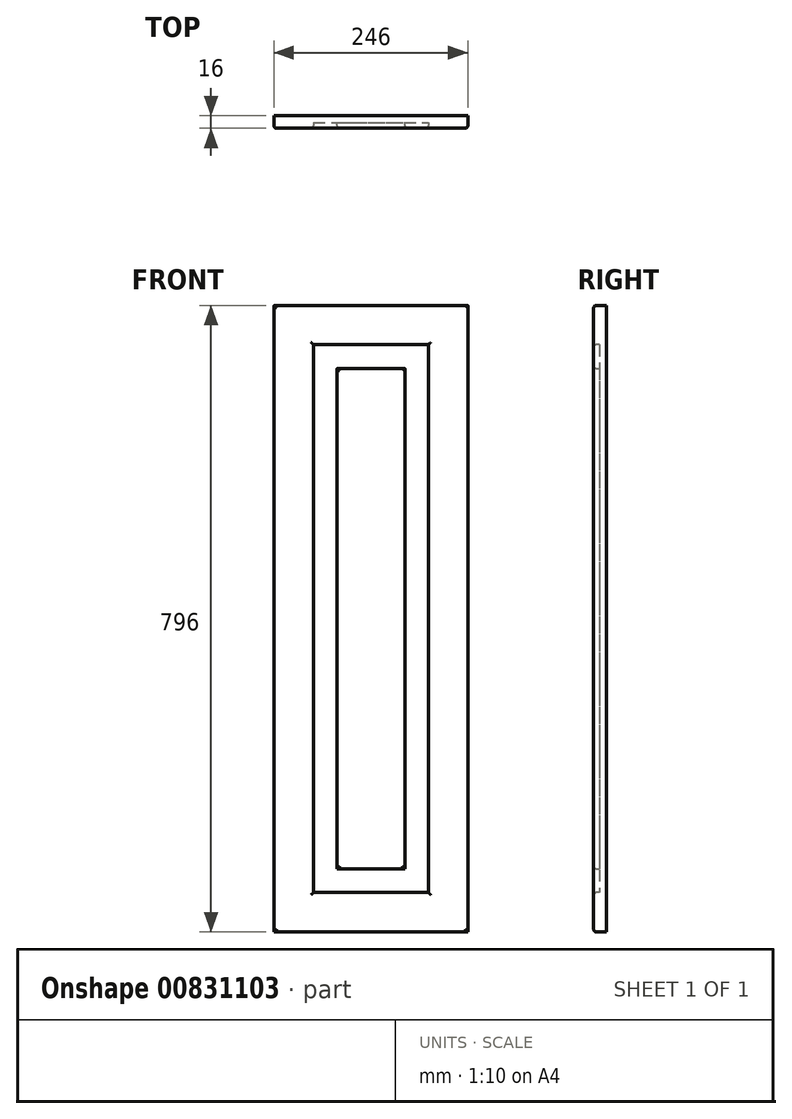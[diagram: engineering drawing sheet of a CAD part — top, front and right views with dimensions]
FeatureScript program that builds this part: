
annotation { "Feature Type Name" : "Feature", "Feature Type Description" : "" }
export const myFeature = defineFeature(function(context is Context, id is Id, definition is map)
    precondition{}
    {
        {
            var Q0;
            Q0=qCreatedBy(makeId("Front.planeOp"),FACE);
            var sketch = newSketch(context, id + "F0", { "sketchPlane" : qUnion([Q0])});
            skLineSegment(sketch, "E0.bottom", {"start": v(0, 0) * mm, "end": v(44.66, 0) * mm});
            skLineSegment(sketch, "E0.top", {"start": v(0, 33.8) * mm, "end": v(44.66, 33.8) * mm});
            skLineSegment(sketch, "E0.left", {"start": v(0, 0) * mm, "end": v(0, 33.8) * mm});
            skLineSegment(sketch, "E0.right", {"start": v(44.66, 0) * mm, "end": v(44.66, 33.8) * mm});
            skSolve(sketch);
        }
        {
            var Q0;
            Q0=makeQuery(id+"F0.imprint","IMPRINT",FACE,{"disambiguationData":[TD([[makeQuery(id+"F0.imprint","IMPRINT",EDGE,{"derivedFrom":sQuery(id+"F0.wireOp",EDGE,"E0.bottom")}),1.0]])]});
            extrude(context, id + "F1", {"entities" : qUnion([Q0]), "depth" : 16 * mm, "offsetDistance" : 25.4 * mm});
        }
        {
            var Q0;
            Q0=makeQuery(id+"F1.opExtrude","SWEPT_FACE",FACE,{"disambiguationData":[OSD([sQuery(id+"F0.wireOp",EDGE,"E0.bottom")])]});
            extrude(context, id + "F2", {"entities" : qUnion([Q0]), "operationType" : NewBodyOperationType.ADD, "oppositeDirection" : true, "depth" : 796 * mm, "offsetDistance" : 25 * mm});
        }
        {
            var Q0;
            {var subQ0=sQuery(id+"F0.wireOp",EDGE,"E0.left");Q0=makeQuery(id+"F2.boolean.opBoolean","MERGE",FACE,{"derivedFrom":[makeQuery(id+"F1.opExtrude","SWEPT_FACE",FACE,{"disambiguationData":[OSD([subQ0])]}),makeQuery(id+"F2.opExtrude","SWEPT_FACE",FACE,{"disambiguationData":[OSD([sQuery(id+"F0.wireOp",EDGE,"E0.bottom"),subQ0])]})]});}
            extrude(context, id + "F3", {"entities" : qUnion([Q0]), "operationType" : NewBodyOperationType.ADD, "oppositeDirection" : true, "depth" : 196 * mm, "offsetDistance" : 25 * mm});
        }
        {
            var Q0;
            {var subQ0=sQuery(id+"F0.wireOp",EDGE,"E0.left");var subQ1=sQuery(id+"F0.wireOp",EDGE,"E0.bottom");Q0=makeQuery(id+"F3.boolean.opBoolean","MERGE",FACE,{"derivedFrom":[makeQuery(id+"F2.boolean.opBoolean","MERGE",FACE,{"derivedFrom":[makeQuery(id+"F1.opExtrude","CAP_FACE",FACE,{"disambiguationData":[OSD([subQ1,sQuery(id+"F0.wireOp",EDGE,"E0.top"),subQ0,sQuery(id+"F0.wireOp",EDGE,"E0.right")])],"isStart":false}),makeQuery(id+"F2.opExtrude","SWEPT_FACE",FACE,{"disambiguationData":[OSD([subQ1]),TDD([makeQuery(id+"F1.opExtrude","CAP_EDGE",EDGE,{"disambiguationData":[OSD([subQ1])],"isStart":false})])]})]}),makeQuery(id+"F3.opExtrude","SWEPT_FACE",FACE,{"disambiguationData":[OSD([subQ1,subQ0]),TDD([makeQuery(id+"F2.boolean.opBoolean","MERGE",EDGE,{"derivedFrom":[makeQuery(id+"F1.opExtrude","CAP_EDGE",EDGE,{"disambiguationData":[OSD([subQ0])],"isStart":false}),makeQuery(id+"F2.opExtrude","SWEPT_EDGE",EDGE,{"disambiguationData":[OSD([subQ1,subQ0]),TDD([makeQuery(id+"F1.opExtrude","CAP_VERTEX",VERTEX,{"disambiguationData":[OSD([subQ1,subQ0])],"isStart":false})])]})]})])]})]});}
            var sketch = newSketch(context, id + "F4", { "sketchPlane" : qUnion([Q0])});
            skLineSegment(sketch, "E1.bottom", {"start": v(59.7, 646.67) * mm, "end": v(128.66, 646.67) * mm});
            skLineSegment(sketch, "E1.top", {"start": v(59.7, 152.97) * mm, "end": v(128.66, 152.97) * mm});
            skLineSegment(sketch, "E1.left", {"start": v(59.7, 646.67) * mm, "end": v(59.7, 152.97) * mm});
            skLineSegment(sketch, "E1.right", {"start": v(128.66, 646.67) * mm, "end": v(128.66, 152.97) * mm});
            skSolve(sketch);
        }
        {
            var Q0;
            Q0=makeQuery(id+"F4.imprint","IMPRINT",FACE,{"disambiguationData":[TD([[makeQuery(id+"F4.imprint","IMPRINT",EDGE,{"derivedFrom":sQuery(id+"F4.wireOp",EDGE,"E1.bottom")}),-1.0]])]});
            extrude(context, id + "F5", {"entities" : qUnion([Q0]), "operationType" : NewBodyOperationType.REMOVE, "oppositeDirection" : true, "depth" : 7 * mm, "offsetDistance" : 25 * mm});
        }
        {
            var Q0;
            Q0=makeQuery(id+"F5.boolean.opBoolean","COPY",FACE,{"derivedFrom":makeQuery(id+"F5.opExtrude","SWEPT_FACE",FACE,{"disambiguationData":[OSD([sQuery(id+"F4.wireOp",EDGE,"E1.left")])]})});
            extrude(context, id + "F6", {"entities" : qUnion([Q0]), "operationType" : NewBodyOperationType.REMOVE, "oppositeDirection" : true, "depth" : 9.7 * mm, "offsetDistance" : 25 * mm});
        }
        {
            var Q0;
            {var subQ0=sQuery(id+"F4.wireOp",EDGE,"E1.bottom");Q0=makeQuery(id+"F6.boolean.opBoolean","MERGE",FACE,{"derivedFrom":[makeQuery(id+"F5.boolean.opBoolean","COPY",FACE,{"derivedFrom":makeQuery(id+"F5.opExtrude","SWEPT_FACE",FACE,{"disambiguationData":[OSD([subQ0])]})}),makeQuery(id+"F6.opExtrude","SWEPT_FACE",FACE,{"disambiguationData":[OSD([subQ0,sQuery(id+"F4.wireOp",EDGE,"E1.left")])]})]});}
            extrude(context, id + "F7", {"entities" : qUnion([Q0]), "operationType" : NewBodyOperationType.ADD, "oppositeDirection" : true, "depth" : 99.33 * mm, "offsetDistance" : 25 * mm});
        }
        {
            var Q0;
            {var subQ0=sQuery(id+"F4.wireOp",EDGE,"E1.bottom");Q0=makeQuery(id+"F6.boolean.opBoolean","MERGE",FACE,{"derivedFrom":[makeQuery(id+"F5.boolean.opBoolean","COPY",FACE,{"derivedFrom":makeQuery(id+"F5.opExtrude","SWEPT_FACE",FACE,{"disambiguationData":[OSD([subQ0])]})}),makeQuery(id+"F6.opExtrude","SWEPT_FACE",FACE,{"disambiguationData":[OSD([subQ0,sQuery(id+"F4.wireOp",EDGE,"E1.left")])]})]});}
            extrude(context, id + "F8", {"entities" : qUnion([Q0]), "operationType" : NewBodyOperationType.REMOVE, "oppositeDirection" : true, "depth" : 99.33 * mm, "offsetDistance" : 25 * mm});
        }
        {
            var Q0;
            {var subQ0=sQuery(id+"F4.wireOp",EDGE,"E1.right");Q0=makeQuery(id+"F8.boolean.opBoolean","MERGE",FACE,{"derivedFrom":[makeQuery(id+"F5.boolean.opBoolean","COPY",FACE,{"derivedFrom":makeQuery(id+"F5.opExtrude","SWEPT_FACE",FACE,{"disambiguationData":[OSD([subQ0])]})}),makeQuery(id+"F8.opExtrude","SWEPT_FACE",FACE,{"disambiguationData":[OSD([sQuery(id+"F4.wireOp",EDGE,"E1.bottom"),subQ0])]})]});}
            extrude(context, id + "F9", {"entities" : qUnion([Q0]), "operationType" : NewBodyOperationType.REMOVE, "oppositeDirection" : true, "depth" : 17.34 * mm, "offsetDistance" : 25 * mm});
        }
        {
            var Q0;
            {var subQ0=sQuery(id+"F4.wireOp",EDGE,"E1.top");Q0=makeQuery(id+"F9.boolean.opBoolean","MERGE",FACE,{"derivedFrom":[makeQuery(id+"F6.boolean.opBoolean","MERGE",FACE,{"derivedFrom":[makeQuery(id+"F5.boolean.opBoolean","COPY",FACE,{"derivedFrom":makeQuery(id+"F5.opExtrude","SWEPT_FACE",FACE,{"disambiguationData":[OSD([subQ0])]})}),makeQuery(id+"F6.opExtrude","SWEPT_FACE",FACE,{"disambiguationData":[OSD([subQ0,sQuery(id+"F4.wireOp",EDGE,"E1.left")])]})]}),makeQuery(id+"F9.opExtrude","SWEPT_FACE",FACE,{"disambiguationData":[OSD([subQ0,sQuery(id+"F4.wireOp",EDGE,"E1.right")])]})]});}
            extrude(context, id + "F10", {"entities" : qUnion([Q0]), "operationType" : NewBodyOperationType.REMOVE, "oppositeDirection" : true, "depth" : 102.97 * mm, "offsetDistance" : 25 * mm});
        }
        {
            var Q0;
            {var subQ0=sQuery(id+"F4.wireOp",EDGE,"E1.right");var subQ1=sQuery(id+"F4.wireOp",EDGE,"E1.top");var subQ2=sQuery(id+"F4.wireOp",EDGE,"E1.left");var subQ3=sQuery(id+"F4.wireOp",EDGE,"E1.bottom");Q0=makeQuery(id+"F10.boolean.opBoolean","MERGE",FACE,{"derivedFrom":[makeQuery(id+"F9.boolean.opBoolean","MERGE",FACE,{"derivedFrom":[makeQuery(id+"F8.boolean.opBoolean","MERGE",FACE,{"derivedFrom":[makeQuery(id+"F6.boolean.opBoolean","MERGE",FACE,{"derivedFrom":[makeQuery(id+"F5.boolean.opBoolean","COPY",FACE,{"derivedFrom":makeQuery(id+"F5.opExtrude","CAP_FACE",FACE,{"disambiguationData":[OSD([subQ3,subQ1,subQ2,subQ0])],"isStart":false})}),makeQuery(id+"F6.opExtrude","SWEPT_FACE",FACE,{"disambiguationData":[OSD([subQ2]),TDD([makeQuery(id+"F5.boolean.opBoolean","COPY",EDGE,{"derivedFrom":makeQuery(id+"F5.opExtrude","CAP_EDGE",EDGE,{"disambiguationData":[OSD([subQ2])],"isStart":false})})])]})]}),makeQuery(id+"F8.opExtrude","SWEPT_FACE",FACE,{"disambiguationData":[OSD([subQ3,subQ2]),TDD([makeQuery(id+"F6.boolean.opBoolean","MERGE",EDGE,{"derivedFrom":[makeQuery(id+"F5.boolean.opBoolean","COPY",EDGE,{"derivedFrom":makeQuery(id+"F5.opExtrude","CAP_EDGE",EDGE,{"disambiguationData":[OSD([subQ3])],"isStart":false})}),makeQuery(id+"F6.opExtrude","SWEPT_EDGE",EDGE,{"disambiguationData":[OSD([subQ3,subQ2]),TDD([makeQuery(id+"F5.boolean.opBoolean","COPY",VERTEX,{"derivedFrom":makeQuery(id+"F5.opExtrude","CAP_VERTEX",VERTEX,{"disambiguationData":[OSD([subQ3,subQ2])],"isStart":false})})])]})]})])]})]}),makeQuery(id+"F9.opExtrude","SWEPT_FACE",FACE,{"disambiguationData":[OSD([subQ3,subQ0]),TDD([makeQuery(id+"F8.boolean.opBoolean","MERGE",EDGE,{"derivedFrom":[makeQuery(id+"F5.boolean.opBoolean","COPY",EDGE,{"derivedFrom":makeQuery(id+"F5.opExtrude","CAP_EDGE",EDGE,{"disambiguationData":[OSD([subQ0])],"isStart":false})}),makeQuery(id+"F8.opExtrude","SWEPT_EDGE",EDGE,{"disambiguationData":[OSD([subQ3,subQ0]),TDD([makeQuery(id+"F5.boolean.opBoolean","COPY",VERTEX,{"derivedFrom":makeQuery(id+"F5.opExtrude","CAP_VERTEX",VERTEX,{"disambiguationData":[OSD([subQ3,subQ0])],"isStart":false})})])]})]})])]})]}),makeQuery(id+"F10.opExtrude","SWEPT_FACE",FACE,{"disambiguationData":[OSD([subQ1,subQ2,subQ0]),TDD([makeQuery(id+"F9.boolean.opBoolean","MERGE",EDGE,{"derivedFrom":[makeQuery(id+"F6.boolean.opBoolean","MERGE",EDGE,{"derivedFrom":[makeQuery(id+"F5.boolean.opBoolean","COPY",EDGE,{"derivedFrom":makeQuery(id+"F5.opExtrude","CAP_EDGE",EDGE,{"disambiguationData":[OSD([subQ1])],"isStart":false})}),makeQuery(id+"F6.opExtrude","SWEPT_EDGE",EDGE,{"disambiguationData":[OSD([subQ1,subQ2]),TDD([makeQuery(id+"F5.boolean.opBoolean","COPY",VERTEX,{"derivedFrom":makeQuery(id+"F5.opExtrude","CAP_VERTEX",VERTEX,{"disambiguationData":[OSD([subQ1,subQ2])],"isStart":false})})])]})]}),makeQuery(id+"F9.opExtrude","SWEPT_EDGE",EDGE,{"disambiguationData":[OSD([subQ1,subQ0]),TDD([makeQuery(id+"F5.boolean.opBoolean","COPY",VERTEX,{"derivedFrom":makeQuery(id+"F5.opExtrude","CAP_VERTEX",VERTEX,{"disambiguationData":[OSD([subQ1,subQ0])],"isStart":false})})])]})]})])]})]});}
            var sketch = newSketch(context, id + "F11", { "sketchPlane" : qUnion([Q0])});
            skLineSegment(sketch, "E2.bottom", {"start": v(74.13, 678.73) * mm, "end": v(109.41, 678.73) * mm});
            skLineSegment(sketch, "E2.top", {"start": v(74.13, 186.63) * mm, "end": v(109.41, 186.63) * mm});
            skLineSegment(sketch, "E2.left", {"start": v(74.13, 678.73) * mm, "end": v(74.13, 186.63) * mm});
            skLineSegment(sketch, "E2.right", {"start": v(109.41, 678.73) * mm, "end": v(109.41, 186.63) * mm});
            skSolve(sketch);
        }
        {
            var Q0;
            Q0=makeQuery(id+"F11.imprint","IMPRINT",FACE,{"disambiguationData":[TD([[makeQuery(id+"F11.imprint","IMPRINT",EDGE,{"derivedFrom":sQuery(id+"F11.wireOp",EDGE,"E2.bottom")}),-1.0]])]});
            extrude(context, id + "F12", {"entities" : qUnion([Q0]), "operationType" : NewBodyOperationType.ADD, "depth" : 7 * mm, "offsetDistance" : 25 * mm});
        }
        {
            var Q0;
            Q0=makeQuery(id+"F12.opExtrude","SWEPT_FACE",FACE,{"disambiguationData":[OSD([sQuery(id+"F11.wireOp",EDGE,"E2.bottom")])]});
            extrude(context, id + "F13", {"entities" : qUnion([Q0]), "operationType" : NewBodyOperationType.ADD, "depth" : 37.27 * mm, "offsetDistance" : 25 * mm});
        }
        {
            var Q0;
            {var subQ0=sQuery(id+"F11.wireOp",EDGE,"E2.right");Q0=makeQuery(id+"F13.boolean.opBoolean","MERGE",FACE,{"derivedFrom":[makeQuery(id+"F12.opExtrude","SWEPT_FACE",FACE,{"disambiguationData":[OSD([subQ0])]}),makeQuery(id+"F13.opExtrude","SWEPT_FACE",FACE,{"disambiguationData":[OSD([sQuery(id+"F11.wireOp",EDGE,"E2.bottom"),subQ0])]})]});}
            extrude(context, id + "F14", {"entities" : qUnion([Q0]), "operationType" : NewBodyOperationType.ADD, "depth" : 6.58 * mm, "offsetDistance" : 25 * mm});
        }
        {
            var Q0;
            {var subQ0=sQuery(id+"F11.wireOp",EDGE,"E2.top");Q0=makeQuery(id+"F14.boolean.opBoolean","MERGE",FACE,{"derivedFrom":[makeQuery(id+"F12.opExtrude","SWEPT_FACE",FACE,{"disambiguationData":[OSD([subQ0])]}),makeQuery(id+"F14.opExtrude","SWEPT_FACE",FACE,{"disambiguationData":[OSD([subQ0,sQuery(id+"F11.wireOp",EDGE,"E2.right")])]})]});}
            extrude(context, id + "F15", {"entities" : qUnion([Q0]), "operationType" : NewBodyOperationType.ADD, "depth" : 106.63 * mm, "offsetDistance" : 25 * mm});
        }
        {
            var Q0;
            {var subQ0=sQuery(id+"F11.wireOp",EDGE,"E2.left");Q0=makeQuery(id+"F15.boolean.opBoolean","MERGE",FACE,{"derivedFrom":[makeQuery(id+"F13.boolean.opBoolean","MERGE",FACE,{"derivedFrom":[makeQuery(id+"F12.opExtrude","SWEPT_FACE",FACE,{"disambiguationData":[OSD([subQ0])]}),makeQuery(id+"F13.opExtrude","SWEPT_FACE",FACE,{"disambiguationData":[OSD([sQuery(id+"F11.wireOp",EDGE,"E2.bottom"),subQ0])]})]}),makeQuery(id+"F15.opExtrude","SWEPT_FACE",FACE,{"disambiguationData":[OSD([sQuery(id+"F11.wireOp",EDGE,"E2.top"),subQ0])]})]});}
            extrude(context, id + "F16", {"entities" : qUnion([Q0]), "operationType" : NewBodyOperationType.REMOVE, "oppositeDirection" : true, "depth" : 5.87 * mm, "offsetDistance" : 25 * mm});
        }
        {
            var Q0;
            Q0=makeQuery(id+"F3.opExtrude","CAP_FACE",FACE,{"disambiguationData":[OSD([sQuery(id+"F0.wireOp",EDGE,"E0.bottom"),sQuery(id+"F0.wireOp",EDGE,"E0.left")])],"isStart":false});
            extrude(context, id + "F17", {"entities" : qUnion([Q0]), "operationType" : NewBodyOperationType.ADD, "depth" : 200 * mm, "offsetDistance" : 25 * mm});
        }
        {
            var Q0;
            {var subQ0=sQuery(id+"F4.wireOp",EDGE,"E1.right");Q0=makeQuery(id+"F10.boolean.opBoolean","MERGE",FACE,{"derivedFrom":[makeQuery(id+"F9.boolean.opBoolean","COPY",FACE,{"derivedFrom":makeQuery(id+"F9.opExtrude","CAP_FACE",FACE,{"disambiguationData":[OSD([sQuery(id+"F4.wireOp",EDGE,"E1.bottom"),subQ0])],"isStart":false})}),makeQuery(id+"F10.opExtrude","SWEPT_FACE",FACE,{"disambiguationData":[OSD([sQuery(id+"F4.wireOp",EDGE,"E1.top"),subQ0])]})]});}
            extrude(context, id + "F18", {"entities" : qUnion([Q0]), "operationType" : NewBodyOperationType.REMOVE, "oppositeDirection" : true, "depth" : 200 * mm, "offsetDistance" : 25 * mm});
        }
        {
            var Q0;
            {var subQ0=sQuery(id+"F11.wireOp",EDGE,"E2.right");var subQ1=sQuery(id+"F11.wireOp",EDGE,"E2.top");Q0=makeQuery(id+"F15.boolean.opBoolean","MERGE",FACE,{"derivedFrom":[makeQuery(id+"F14.opExtrude","CAP_FACE",FACE,{"disambiguationData":[OSD([sQuery(id+"F11.wireOp",EDGE,"E2.bottom"),subQ0])],"isStart":false}),makeQuery(id+"F15.opExtrude","SWEPT_FACE",FACE,{"disambiguationData":[OSD([subQ1,subQ0]),TDD([makeQuery(id+"F14.opExtrude","CAP_EDGE",EDGE,{"disambiguationData":[OSD([subQ1,subQ0])],"isStart":false})])]})]});}
            extrude(context, id + "F19", {"entities" : qUnion([Q0]), "operationType" : NewBodyOperationType.ADD, "depth" : 200 * mm, "offsetDistance" : 25 * mm});
        }
        {
            var Q0;
            Q0=makeQuery(id+"F17.opExtrude","CAP_FACE",FACE,{"disambiguationData":[OSD([sQuery(id+"F0.wireOp",EDGE,"E0.bottom"),sQuery(id+"F0.wireOp",EDGE,"E0.left")])],"isStart":false});
            extrude(context, id + "F20", {"entities" : qUnion([Q0]), "operationType" : NewBodyOperationType.ADD, "depth" : 200 * mm, "offsetDistance" : 25 * mm});
        }
        {
            var Q0;
            Q0=makeQuery(id+"F18.boolean.opBoolean","COPY",FACE,{"derivedFrom":makeQuery(id+"F18.opExtrude","CAP_FACE",FACE,{"disambiguationData":[OSD([sQuery(id+"F4.wireOp",EDGE,"E1.bottom"),sQuery(id+"F4.wireOp",EDGE,"E1.top"),sQuery(id+"F4.wireOp",EDGE,"E1.right")])],"isStart":false})});
            extrude(context, id + "F21", {"entities" : qUnion([Q0]), "operationType" : NewBodyOperationType.REMOVE, "oppositeDirection" : true, "depth" : 200 * mm, "offsetDistance" : 25 * mm});
        }
        {
            var Q0;
            Q0=makeQuery(id+"F19.opExtrude","CAP_FACE",FACE,{"disambiguationData":[OSD([sQuery(id+"F11.wireOp",EDGE,"E2.bottom"),sQuery(id+"F11.wireOp",EDGE,"E2.top"),sQuery(id+"F11.wireOp",EDGE,"E2.right")])],"isStart":false});
            extrude(context, id + "F22", {"entities" : qUnion([Q0]), "operationType" : NewBodyOperationType.ADD, "depth" : 200 * mm, "offsetDistance" : 25 * mm});
        }
        {
            var Q0;
            Q0=makeQuery(id+"F22.opExtrude","CAP_FACE",FACE,{"disambiguationData":[OSD([sQuery(id+"F11.wireOp",EDGE,"E2.bottom"),sQuery(id+"F11.wireOp",EDGE,"E2.top"),sQuery(id+"F11.wireOp",EDGE,"E2.right")])],"isStart":false});
            extrude(context, id + "F23", {"entities" : qUnion([Q0]), "operationType" : NewBodyOperationType.REMOVE, "oppositeDirection" : true, "depth" : 350 * mm, "offsetDistance" : 25 * mm});
        }
        {
            var Q0;
            Q0=makeQuery(id+"F21.boolean.opBoolean","COPY",FACE,{"derivedFrom":makeQuery(id+"F21.opExtrude","CAP_FACE",FACE,{"disambiguationData":[OSD([sQuery(id+"F4.wireOp",EDGE,"E1.bottom"),sQuery(id+"F4.wireOp",EDGE,"E1.top"),sQuery(id+"F4.wireOp",EDGE,"E1.right")])],"isStart":false})});
            extrude(context, id + "F24", {"entities" : qUnion([Q0]), "operationType" : NewBodyOperationType.ADD, "depth" : 350 * mm, "offsetDistance" : 25 * mm});
        }
        {
            var Q0;
            Q0=makeQuery(id+"F20.opExtrude","CAP_FACE",FACE,{"disambiguationData":[OSD([sQuery(id+"F0.wireOp",EDGE,"E0.bottom"),sQuery(id+"F0.wireOp",EDGE,"E0.left")])],"isStart":false});
            extrude(context, id + "F25", {"entities" : qUnion([Q0]), "operationType" : NewBodyOperationType.REMOVE, "oppositeDirection" : true, "depth" : 350 * mm, "offsetDistance" : 25 * mm});
        }
        {
            var Q0;
            {var subQ0=sQuery(id+"F11.wireOp",EDGE,"E2.right");var subQ1=sQuery(id+"F11.wireOp",EDGE,"E2.top");var subQ2=makeQuery(id+"F12.opExtrude","CAP_VERTEX",VERTEX,{"disambiguationData":[OSD([subQ1,subQ0])],"isStart":false});var subQ3=sQuery(id+"F11.wireOp",EDGE,"E2.bottom");var subQ4=makeQuery(id+"F13.boolean.opBoolean","MERGE",EDGE,{"derivedFrom":[makeQuery(id+"F12.opExtrude","CAP_EDGE",EDGE,{"disambiguationData":[OSD([subQ0])],"isStart":false}),makeQuery(id+"F13.opExtrude","SWEPT_EDGE",EDGE,{"disambiguationData":[OSD([subQ3,subQ0]),TDD([makeQuery(id+"F12.opExtrude","CAP_VERTEX",VERTEX,{"disambiguationData":[OSD([subQ3,subQ0])],"isStart":false})])]})]});var subQ5=makeQuery(id+"F15.boolean.opBoolean","MERGE",EDGE,{"derivedFrom":[makeQuery(id+"F14.opExtrude","CAP_EDGE",EDGE,{"disambiguationData":[OSD([subQ3,subQ0]),TDD([subQ4])],"isStart":false}),makeQuery(id+"F15.opExtrude","SWEPT_EDGE",EDGE,{"disambiguationData":[OSD([subQ1,subQ0]),TDD([makeQuery(id+"F14.opExtrude","CAP_VERTEX",VERTEX,{"disambiguationData":[OSD([subQ1,subQ0]),TDD([subQ2])],"isStart":false})])]})]});Q0=makeQuery(id+"F22.boolean.opBoolean","MERGE",FACE,{"derivedFrom":[makeQuery(id+"F19.boolean.opBoolean","MERGE",FACE,{"derivedFrom":[makeQuery(id+"F15.boolean.opBoolean","MERGE",FACE,{"derivedFrom":[makeQuery(id+"F14.boolean.opBoolean","MERGE",FACE,{"derivedFrom":[makeQuery(id+"F13.boolean.opBoolean","MERGE",FACE,{"derivedFrom":[makeQuery(id+"F12.opExtrude","CAP_FACE",FACE,{"disambiguationData":[OSD([subQ3,subQ1,sQuery(id+"F11.wireOp",EDGE,"E2.left"),subQ0])],"isStart":false}),makeQuery(id+"F13.opExtrude","SWEPT_FACE",FACE,{"disambiguationData":[OSD([subQ3]),TDD([makeQuery(id+"F12.opExtrude","CAP_EDGE",EDGE,{"disambiguationData":[OSD([subQ3])],"isStart":false})])]})]}),makeQuery(id+"F14.opExtrude","SWEPT_FACE",FACE,{"disambiguationData":[OSD([subQ3,subQ0]),TDD([subQ4])]})]}),makeQuery(id+"F15.opExtrude","SWEPT_FACE",FACE,{"disambiguationData":[OSD([subQ1,subQ0]),TDD([makeQuery(id+"F14.boolean.opBoolean","MERGE",EDGE,{"derivedFrom":[makeQuery(id+"F12.opExtrude","CAP_EDGE",EDGE,{"disambiguationData":[OSD([subQ1])],"isStart":false}),makeQuery(id+"F14.opExtrude","SWEPT_EDGE",EDGE,{"disambiguationData":[OSD([subQ1,subQ0]),TDD([subQ2])]})]})])]})]}),makeQuery(id+"F19.opExtrude","SWEPT_FACE",FACE,{"disambiguationData":[OSD([subQ3,subQ1,subQ0]),TDD([subQ5])]})]}),makeQuery(id+"F22.opExtrude","SWEPT_FACE",FACE,{"disambiguationData":[OSD([subQ3,subQ1,subQ0]),TDD([makeQuery(id+"F19.opExtrude","CAP_EDGE",EDGE,{"disambiguationData":[OSD([subQ3,subQ1,subQ0]),TDD([subQ5])],"isStart":false})])]})]});}
            var Q1;
            {var subQ0=sQuery(id+"F4.wireOp",EDGE,"E1.right");var subQ1=sQuery(id+"F4.wireOp",EDGE,"E1.top");var subQ2=sQuery(id+"F4.wireOp",EDGE,"E1.bottom");var subQ3=sQuery(id+"F0.wireOp",EDGE,"E0.left");var subQ4=sQuery(id+"F0.wireOp",EDGE,"E0.bottom");var subQ5=makeQuery(id+"F2.boolean.opBoolean","MERGE",EDGE,{"derivedFrom":[makeQuery(id+"F1.opExtrude","CAP_EDGE",EDGE,{"disambiguationData":[OSD([subQ3])],"isStart":false}),makeQuery(id+"F2.opExtrude","SWEPT_EDGE",EDGE,{"disambiguationData":[OSD([subQ4,subQ3]),TDD([makeQuery(id+"F1.opExtrude","CAP_VERTEX",VERTEX,{"disambiguationData":[OSD([subQ4,subQ3])],"isStart":false})])]})]});var subQ6=makeQuery(id+"F3.opExtrude","CAP_EDGE",EDGE,{"disambiguationData":[OSD([subQ4,subQ3]),TDD([subQ5])],"isStart":false});Q1=makeQuery(id+"F24.boolean.opBoolean","MERGE",FACE,{"derivedFrom":[makeQuery(id+"F20.boolean.opBoolean","MERGE",FACE,{"derivedFrom":[makeQuery(id+"F17.boolean.opBoolean","MERGE",FACE,{"derivedFrom":[makeQuery(id+"F3.boolean.opBoolean","MERGE",FACE,{"derivedFrom":[makeQuery(id+"F2.boolean.opBoolean","MERGE",FACE,{"derivedFrom":[makeQuery(id+"F1.opExtrude","CAP_FACE",FACE,{"disambiguationData":[OSD([subQ4,sQuery(id+"F0.wireOp",EDGE,"E0.top"),subQ3,sQuery(id+"F0.wireOp",EDGE,"E0.right")])],"isStart":false}),makeQuery(id+"F2.opExtrude","SWEPT_FACE",FACE,{"disambiguationData":[OSD([subQ4]),TDD([makeQuery(id+"F1.opExtrude","CAP_EDGE",EDGE,{"disambiguationData":[OSD([subQ4])],"isStart":false})])]})]}),makeQuery(id+"F3.opExtrude","SWEPT_FACE",FACE,{"disambiguationData":[OSD([subQ4,subQ3]),TDD([subQ5])]})]}),makeQuery(id+"F17.opExtrude","SWEPT_FACE",FACE,{"disambiguationData":[OSD([subQ4,subQ3]),TDD([subQ6])]})]}),makeQuery(id+"F20.opExtrude","SWEPT_FACE",FACE,{"disambiguationData":[OSD([subQ4,subQ3]),TDD([makeQuery(id+"F17.opExtrude","CAP_EDGE",EDGE,{"disambiguationData":[OSD([subQ4,subQ3]),TDD([subQ6])],"isStart":false})])]})]}),makeQuery(id+"F24.opExtrude","SWEPT_FACE",FACE,{"disambiguationData":[OSD([subQ2,subQ1,subQ0]),TDD([makeQuery(id+"F21.boolean.opBoolean","COPY",EDGE,{"derivedFrom":makeQuery(id+"F21.opExtrude","CAP_EDGE",EDGE,{"disambiguationData":[OSD([subQ2,subQ1,subQ0]),TDD([makeQuery(id+"F18.boolean.opBoolean","COPY",EDGE,{"derivedFrom":makeQuery(id+"F18.opExtrude","CAP_EDGE",EDGE,{"disambiguationData":[OSD([subQ2,subQ1,subQ0]),TDD([makeQuery(id+"F10.boolean.opBoolean","MERGE",EDGE,{"derivedFrom":[makeQuery(id+"F9.boolean.opBoolean","COPY",EDGE,{"derivedFrom":makeQuery(id+"F9.opExtrude","CAP_EDGE",EDGE,{"disambiguationData":[OSD([subQ2,subQ0]),TDD([makeQuery(id+"F8.boolean.opBoolean","MERGE",EDGE,{"derivedFrom":[makeQuery(id+"F5.boolean.opBoolean","COPY",EDGE,{"derivedFrom":makeQuery(id+"F5.opExtrude","CAP_EDGE",EDGE,{"disambiguationData":[OSD([subQ0])],"isStart":true})}),makeQuery(id+"F8.opExtrude","SWEPT_EDGE",EDGE,{"disambiguationData":[OSD([subQ2,subQ0]),TDD([makeQuery(id+"F5.boolean.opBoolean","COPY",VERTEX,{"derivedFrom":makeQuery(id+"F5.opExtrude","CAP_VERTEX",VERTEX,{"disambiguationData":[OSD([subQ2,subQ0])],"isStart":true})})])]})]})])],"isStart":false})}),makeQuery(id+"F10.opExtrude","SWEPT_EDGE",EDGE,{"disambiguationData":[OSD([subQ1,subQ0]),TDD([makeQuery(id+"F9.boolean.opBoolean","COPY",VERTEX,{"derivedFrom":makeQuery(id+"F9.opExtrude","CAP_VERTEX",VERTEX,{"disambiguationData":[OSD([subQ1,subQ0]),TDD([makeQuery(id+"F5.boolean.opBoolean","COPY",VERTEX,{"derivedFrom":makeQuery(id+"F5.opExtrude","CAP_VERTEX",VERTEX,{"disambiguationData":[OSD([subQ1,subQ0])],"isStart":true})})])],"isStart":false})})])]})]})])],"isStart":false})})])],"isStart":false})})])]})]});}
            fillet(context, id + "F26", {"entities" : qUnion([Q0, Q1]), "radius" : 3 * mm, "tangentPropagation" : true, "allowEdgeOverflow" : false});
        }
    });
